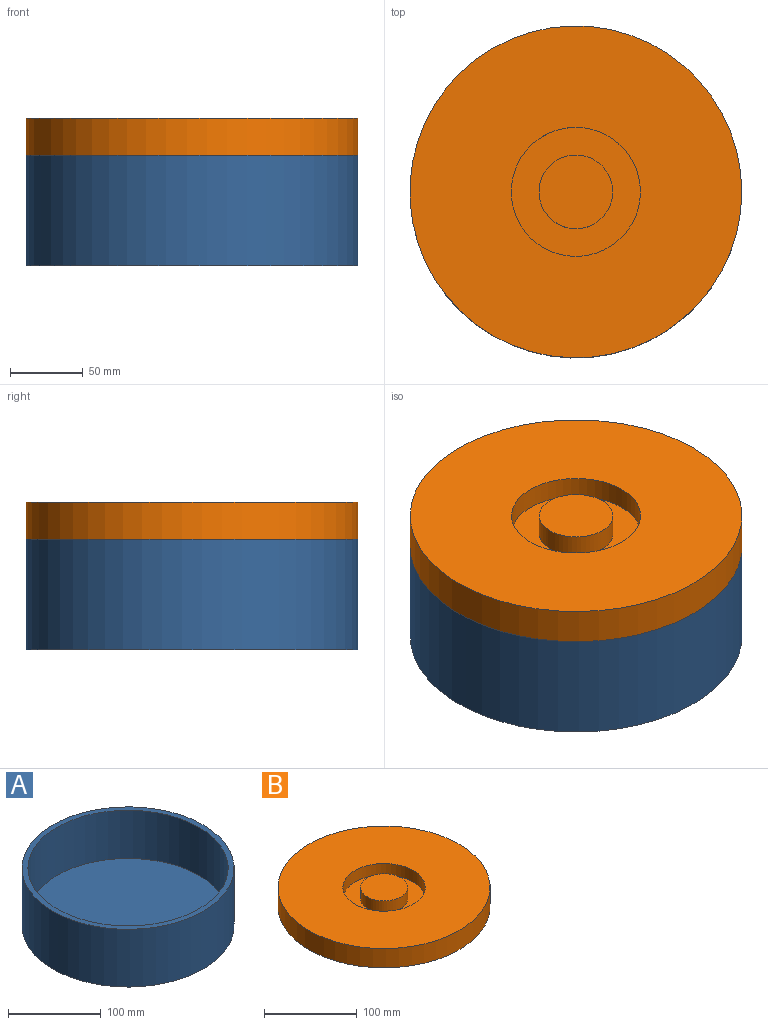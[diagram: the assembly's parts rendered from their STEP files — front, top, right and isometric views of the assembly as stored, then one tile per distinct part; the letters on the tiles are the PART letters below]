
ASSEMBLY  parts=2 mates=1
PART A: 5 faces, bbox 228.6x228.6x76.2 mm
  f0: cylinder r=114.3mm len=228.6mm, axis (0,0,-1), area 54724.4mm2, adj f1,f2
  f1: plane 228.6x228.6mm, normal (0,0,1), area 4433.7mm2, adj f0,f3
  f2: plane 228.6x228.6mm, normal (0,0,-1), area 41043.3mm2, adj f0
  f3: cylinder r=107.95mm len=215.9mm, axis (0,0,1), area 43070.1mm2, adj f1,f4
  f4: plane 215.9x215.9mm, normal (0,0,1), area 36609.6mm2, adj f3
PART B: 9 faces, bbox 228.6x228.6x30.7 mm
  f0: cylinder r=106.68mm len=213.36mm, axis (0,0,-1), area 3575.3mm2, adj f1,f4
  f1: plane 213.36x213.36mm, normal (0,0,-1), area 35753.3mm2, adj f0
  f2: cylinder r=114.3mm len=228.6mm, axis (0,0,-1), area 18241.5mm2, adj f3,f4
  f3: plane 228.6x228.6mm, normal (0,0,1), area 34836.1mm2, adj f2,f6
  f4: plane 228.6x228.6mm, normal (0,0,-1), area 5290mm2, adj f0,f2
  f5: cylinder r=25.4mm len=50.8mm, axis (0,0,1), area 2432.2mm2, adj f7,f8
  f6: cylinder r=44.45mm len=88.9mm, axis (0,0,1), area 4256.3mm2, adj f3,f7
  f7: plane 88.9x88.9mm, normal (0,0,1), area 4180.3mm2, adj f5,f6
  f8: plane 50.8x50.8mm, normal (0,0,1), area 2026.8mm2, adj f5
PLACE A t=(23.79,1.33,-83.32)mm
PLACE B t=(23.79,1.33,-83.58)mm
MATE slider A.f0 <-> B.f0  axis (0,0,1) through (23.79,1.33,-7.12)mm
